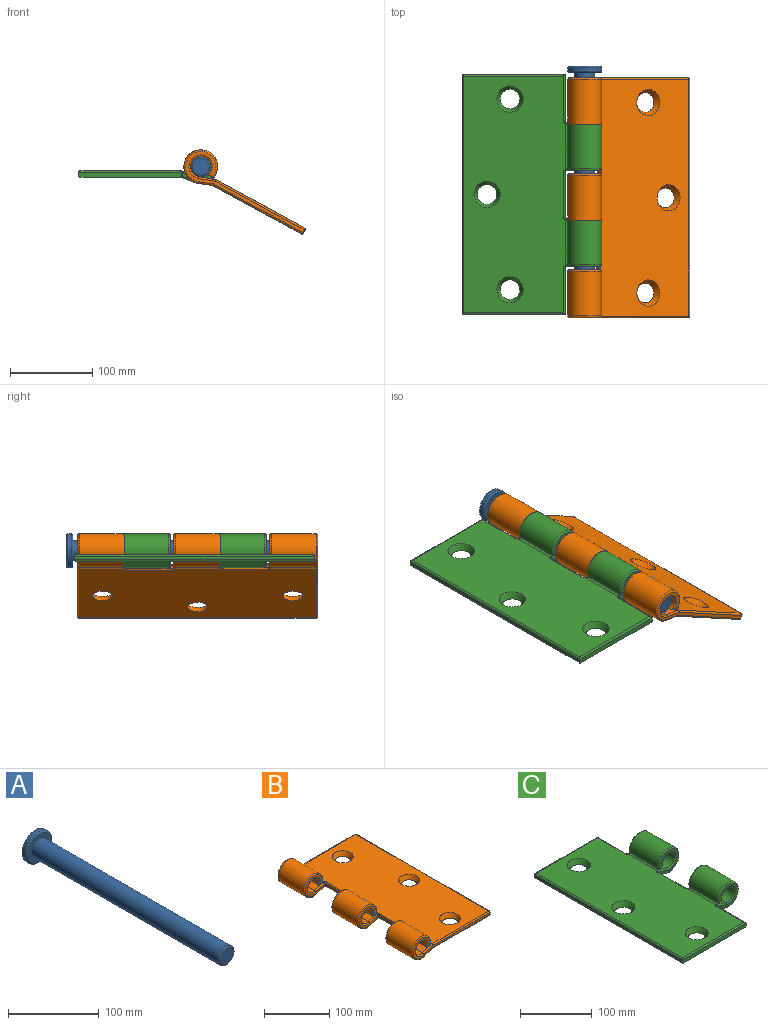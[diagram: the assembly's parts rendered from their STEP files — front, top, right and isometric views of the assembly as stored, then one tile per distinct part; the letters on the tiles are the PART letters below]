
ASSEMBLY  parts=3 mates=2
PART A: 8 faces, bbox 44.4x300x44.4 mm
  f0: cylinder r=12.25mm len=290mm, axis (0,1,0), area 22321mm2, adj f4,f7
  f1: plane 20.5x20.5mm, normal (0,-1,0), area 330.1mm2, adj f7
  f2: cylinder r=20.5mm len=41mm, axis (0,-1,0), area 515.2mm2, adj f5,f6
  f3: plane 37x37mm, normal (0,1,0), area 1075.2mm2, adj f6
  f4: plane 37x37mm, normal (0,-1,0), area 603.8mm2, adj f0,f5
  f5: torus R=18.5mm, axis (0,1,0), area 390.3mm2, adj f2,f4
  f6: torus R=18.5mm, axis (0,1,0), area 390.3mm2, adj f2,f3
  f7: torus R=10.25mm, axis (0,1,0), area 227.5mm2, adj f0,f1
PART B: 95 faces, bbox 171.6x292.4x44.8 mm
  f0: plane 55.23x16.89mm, normal (0.35,0,-0.94), area 979.8mm2, adj f2,f6,f48,f50,f67,f69
  f1: plane 57.36x19.94mm, normal (-0.32,0,0.95), area 1149.3mm2, adj f10,f13,f36,f38,f40,f57,f59
  f2: plane 288.45x123.49mm, normal (0,0,-1), area 33934.5mm2, adj f0,f3,f4,f20,f21,f22,f47,f49
  f3: plane 54.55x16.89mm, normal (0.35,0,-0.94), area 979.3mm2, adj f2,f5,f45,f47,f77
  f4: plane 55.08x16.89mm, normal (0.35,0,-0.94), area 979.7mm2, adj f2,f15,f66,f68,f87
  f5: cylinder r=20.5mm len=54.4mm, axis (0,1,0), area 5924.3mm2, adj f3,f7,f43,f75
  f6: cylinder r=20.5mm len=54.4mm, axis (0,1,0), area 5924.3mm2, adj f0,f8,f46,f65
  f7: plane 54.4x8.42mm, normal (0,0,-1), area 458.3mm2, adj f5,f9,f41,f73
  f8: plane 54.4x8.42mm, normal (0,0,-1), area 458.3mm2, adj f6,f10,f44,f63
  f9: cylinder r=12.5mm len=54.4mm, axis (0,1,0), area 3708.6mm2, adj f7,f11,f39,f74
  f10: cylinder r=12.5mm len=54.4mm, axis (0,1,0), area 3708.6mm2, adj f1,f8,f42,f61
  f11: plane 55.16x19.94mm, normal (-0.32,0,0.95), area 1146.9mm2, adj f9,f13,f33,f35,f37,f76
  f12: plane 56.6x19.94mm, normal (-0.32,0,0.95), area 1148.6mm2, adj f13,f17,f56,f58,f84
  f13: plane 288.06x123.06mm, normal (0,0,1), area 32879mm2, adj f1,f11,f12,f20,f21,f22,f33,f34
  f14: plane 288x4mm, normal (1,0,0), area 1152mm2, adj f81,f89,f90,f94
  f15: cylinder r=20.5mm len=54.4mm, axis (0,1,0), area 5924.3mm2, adj f4,f16,f64,f83
  f16: plane 54.4x8.42mm, normal (0,0,-1), area 458.3mm2, adj f15,f17,f62,f78
  f17: cylinder r=12.5mm len=54.4mm, axis (0,1,0), area 3708.6mm2, adj f12,f16,f60,f79
  f18: plane 165.48x37mm, normal (0,-1,0), area 911.5mm2, adj f78,f79,f83,f84,f87,f88,f91,f94
  f19: plane 165.48x37mm, normal (0,1,0), area 911.5mm2, adj f73,f74,f75,f76,f77,f80,f81,f82
  f20: cone r=12mm half-angle=26.6deg, axis (0,0,1), area 786.8mm2, adj f2,f13
  f21: cone r=12mm half-angle=26.6deg, axis (0,0,1), area 786.8mm2, adj f2,f13
  f22: cone r=12mm half-angle=26.6deg, axis (0,0,1), area 786.8mm2, adj f2,f13
  f23: plane 54.4x4mm, normal (-1,0,0), area 217.6mm2, adj f31,f32,f34,f51
  f24: plane 40.71x37mm, normal (0,-1,0), area 412.7mm2, adj f31,f37,f39,f41,f43,f45
  f25: plane 40.71x37mm, normal (0,1,0), area 412.7mm2, adj f32,f40,f42,f44,f46,f48
  f26: plane 54.4x4.63mm, normal (-1,0,0), area 251.8mm2, adj f29,f30,f53,f72
  f27: plane 39.56x37mm, normal (0,-1,0), area 408.4mm2, adj f29,f59,f61,f63,f65,f67
  f28: plane 39.56x37mm, normal (0,1,0), area 408.4mm2, adj f30,f58,f60,f62,f64,f66
  f29: cylinder r=2mm len=5.26mm, axis (0,0,-1), area 12.7mm2, adj f26,f27,f55,f57,f69,f71
  f30: cylinder r=2mm len=5.26mm, axis (0,0,1), area 12.7mm2, adj f26,f28,f54,f56,f68,f70
  f31: cylinder r=2mm len=4.52mm, axis (0,0,-1), area 12.4mm2, adj f23,f24,f33,f35,f47,f49
  f32: cylinder r=2mm len=4.52mm, axis (0,0,1), area 12.4mm2, adj f23,f25,f36,f38,f50,f52
  f33: torus R=4mm, axis (0,0,-1), area 9.3mm2, adj f11,f13,f31,f34,f35
  f34: cylinder r=2mm len=54.4mm, axis (0,-1,0), area 170.9mm2, adj f13,f23,f33,f36
  f35: bspline ~2.7x2.38mm, area 5.5mm2, adj f11,f31,f33,f37
  f36: torus R=4mm, axis (0,0,-1), area 9.3mm2, adj f1,f13,f32,f34,f38
  f37: cylinder r=2mm len=18.16mm, axis (0.95,0,0.32), area 58.1mm2, adj f11,f24,f35,f39
  f38: bspline ~2.7x2.38mm, area 5.5mm2, adj f1,f32,f36,f40
  f39: torus R=14.5mm, axis (0,-1,0), area 222.3mm2, adj f9,f24,f37,f41
  f40: cylinder r=2mm len=18.16mm, axis (-0.95,0,-0.32), area 58.1mm2, adj f1,f25,f38,f42
  f41: cylinder r=2mm len=8.42mm, axis (-1,0,0), area 19.6mm2, adj f7,f24,f39,f43
  f42: torus R=14.5mm, axis (0,-1,0), area 222.3mm2, adj f10,f25,f40,f44
  f43: torus R=18.5mm, axis (0,-1,0), area 327.5mm2, adj f5,f24,f41,f45
  f44: cylinder r=2mm len=8.42mm, axis (1,0,0), area 19.6mm2, adj f8,f25,f42,f46
  f45: cylinder r=2mm len=16.49mm, axis (-0.94,0,-0.35), area 52.9mm2, adj f3,f24,f43,f47
  f46: torus R=18.5mm, axis (0,-1,0), area 327.5mm2, adj f6,f25,f44,f48
  f47: bspline ~2.4x2.13mm, area 2.8mm2, adj f2,f3,f31,f45,f49
  f48: cylinder r=2mm len=16.49mm, axis (0.94,0,0.35), area 52.9mm2, adj f0,f25,f46,f50
  f49: torus R=4mm, axis (0,0,1), area 9.7mm2, adj f2,f31,f47,f51
  f50: bspline ~2.4x2.13mm, area 2.8mm2, adj f0,f2,f32,f48,f52
  f51: cylinder r=2mm len=54.4mm, axis (0,1,0), area 170.9mm2, adj f2,f23,f49,f52
  f52: torus R=4mm, axis (0,0,1), area 9.7mm2, adj f2,f32,f50,f51
  f53: cylinder r=2mm len=54.4mm, axis (0,-1,0), area 109.1mm2, adj f13,f26,f54,f55
  f54: bspline ~2.37x1.92mm, area 2.8mm2, adj f13,f30,f53,f56
  f55: bspline ~2.37x1.92mm, area 2.8mm2, adj f13,f29,f53,f57
  f56: bspline ~3.57x3.12mm, area 9.3mm2, adj f12,f30,f54,f58
  f57: bspline ~3.94x3.32mm, area 9.3mm2, adj f1,f29,f55,f59
  f58: cylinder r=2mm len=17.01mm, axis (-0.95,0,-0.32), area 54.3mm2, adj f12,f28,f56,f60
  f59: cylinder r=2mm len=17.01mm, axis (0.95,0,0.32), area 54.3mm2, adj f1,f27,f57,f61
  f60: torus R=14.5mm, axis (0,-1,0), area 222.3mm2, adj f17,f28,f58,f62
  f61: torus R=14.5mm, axis (0,-1,0), area 222.3mm2, adj f10,f27,f59,f63
  f62: cylinder r=2mm len=8.42mm, axis (1,0,0), area 19.6mm2, adj f16,f28,f60,f64
  f63: cylinder r=2mm len=8.42mm, axis (-1,0,0), area 19.6mm2, adj f8,f27,f61,f65
  f64: torus R=18.5mm, axis (0,-1,0), area 327.5mm2, adj f15,f28,f62,f66
  f65: torus R=18.5mm, axis (0,-1,0), area 327.5mm2, adj f6,f27,f63,f67
  f66: cylinder r=2mm len=15.35mm, axis (0.94,0,0.35), area 49.1mm2, adj f4,f28,f64,f68
  f67: cylinder r=2mm len=15.35mm, axis (-0.94,0,-0.35), area 49.1mm2, adj f0,f27,f65,f69
  f68: bspline ~3.61x3.08mm, area 5.9mm2, adj f4,f30,f66,f70
  f69: bspline ~3.61x3.08mm, area 5.9mm2, adj f0,f29,f67,f71
  f70: bspline ~3.87x2.48mm, area 5.3mm2, adj f2,f30,f68,f72
  f71: bspline ~3.87x2.48mm, area 5.3mm2, adj f2,f29,f69,f72
  f72: cylinder r=2mm len=54.4mm, axis (0,1,0), area 109.1mm2, adj f2,f26,f70,f71
  f73: cylinder r=2mm len=8.42mm, axis (-1,0,0), area 19.6mm2, adj f7,f19,f74,f75
  f74: torus R=14.5mm, axis (0,-1,0), area 222.3mm2, adj f9,f19,f73,f76
  f75: torus R=18.5mm, axis (0,-1,0), area 327.5mm2, adj f5,f19,f73,f77
  f76: cylinder r=2mm len=20.58mm, axis (0.95,0,0.32), area 65.7mm2, adj f11,f19,f74,f80
  f77: cylinder r=2mm len=17.91mm, axis (-0.94,0,-0.35), area 57.1mm2, adj f3,f19,f75,f82
  f78: cylinder r=2mm len=8.42mm, axis (1,0,0), area 19.6mm2, adj f16,f18,f79,f83
  f79: torus R=14.5mm, axis (0,-1,0), area 222.3mm2, adj f17,f18,f78,f84
  f80: cylinder r=2mm len=123mm, axis (1,0,0), area 385.9mm2, adj f13,f19,f76,f85
  f81: cylinder r=2mm len=4mm, axis (0,0,-1), area 12.6mm2, adj f14,f19,f85,f86
  f82: cylinder r=2mm len=123.36mm, axis (-1,0,0), area 387mm2, adj f2,f19,f77,f86
  f83: torus R=18.5mm, axis (0,-1,0), area 327.5mm2, adj f15,f18,f78,f87
  f84: cylinder r=2mm len=20.58mm, axis (-0.95,0,-0.32), area 65.7mm2, adj f12,f18,f79,f88
  f85: sphere r=2mm, area 6.3mm2, adj f80,f81,f89
  f86: sphere r=2mm, area 4mm2, adj f81,f82,f90
  f87: cylinder r=2mm len=17.91mm, axis (0.94,0,0.35), area 57.1mm2, adj f4,f18,f83,f91
  f88: cylinder r=2mm len=123mm, axis (-1,0,0), area 385.9mm2, adj f13,f18,f84,f92
  f89: cylinder r=2mm len=288mm, axis (0,1,0), area 904.8mm2, adj f13,f14,f85,f92
  f90: cylinder r=2mm len=288mm, axis (0,1,0), area 904.8mm2, adj f2,f14,f86,f93
  f91: cylinder r=2mm len=123.36mm, axis (1,0,0), area 387mm2, adj f2,f18,f87,f93
  f92: sphere r=2mm, area 6.3mm2, adj f88,f89,f94
  f93: sphere r=2mm, area 6.3mm2, adj f90,f91,f94
  f94: cylinder r=2mm len=4mm, axis (0,0,1), area 12.6mm2, adj f14,f18,f92,f93
PART C: 76 faces, bbox 171.2x292x44.4 mm
  f0: plane 54.84x16.89mm, normal (-0.35,0,-0.94), area 979.4mm2, adj f2,f12,f54,f55,f73,f75
  f1: plane 54.84x16.89mm, normal (-0.35,0,-0.94), area 979.4mm2, adj f3,f12,f31,f32,f66,f68
  f2: cylinder r=20.5mm len=54.4mm, axis (0,1,0), area 5924.3mm2, adj f0,f4,f52,f71
  f3: cylinder r=20.5mm len=54.4mm, axis (0,1,0), area 5924.3mm2, adj f1,f5,f33,f64
  f4: plane 54.4x8.42mm, normal (0,0,-1), area 458.3mm2, adj f2,f6,f50,f69
  f5: plane 54.4x8.42mm, normal (0,0,-1), area 458.3mm2, adj f3,f7,f34,f62
  f6: cylinder r=12.5mm len=54.4mm, axis (0,1,0), area 3708.6mm2, adj f4,f8,f48,f67
  f7: cylinder r=12.5mm len=54.4mm, axis (0,1,0), area 3708.6mm2, adj f5,f9,f35,f60
  f8: plane 56.23x19.94mm, normal (0.32,0,0.95), area 1148mm2, adj f6,f13,f44,f45,f46,f61,f63,f65
  f9: plane 56.23x19.94mm, normal (0.32,0,0.95), area 1148mm2, adj f7,f13,f36,f37,f38,f56,f57,f58
  f10: plane 125x6mm, normal (0,-1,0), area 748.3mm2, adj f11,f12,f19,f29,f40,f47
  f11: plane 292x4mm, normal (-1,0,0), area 1168mm2, adj f10,f14,f41,f47
  f12: plane 290x123.06mm, normal (0,0,-1), area 33962.8mm2, adj f0,f1,f10,f15,f16,f17,f29,f30
  f13: plane 288x123mm, normal (0,0,1), area 32665.2mm2, adj f8,f9,f15,f16,f17,f38,f39,f40
  f14: plane 125x4mm, normal (0,1,0), area 500mm2, adj f11,f24,f42,f49
  f15: cone r=12mm half-angle=26.6deg, axis (0,0,1), area 786.8mm2, adj f12,f13
  f16: cone r=12mm half-angle=26.6deg, axis (0,0,1), area 786.8mm2, adj f12,f13
  f17: cone r=12mm half-angle=26.6deg, axis (0,0,1), area 786.8mm2, adj f12,f13
  f18: plane 40.48x37mm, normal (0,-1,0), area 411.9mm2, adj f25,f32,f33,f34,f35,f36
  f19: plane 56.4x4mm, normal (1,0,0), area 225.6mm2, adj f10,f25,f29,f39
  f20: plane 40.48x37mm, normal (0,-1,0), area 411.9mm2, adj f26,f65,f67,f69,f71,f73
  f21: plane 40.48x37mm, normal (0,1,0), area 411.9mm2, adj f27,f58,f60,f62,f64,f66
  f22: plane 54.4x4mm, normal (1,0,0), area 217.6mm2, adj f26,f27,f59,f72
  f23: plane 40.48x37mm, normal (0,1,0), area 411.9mm2, adj f28,f46,f48,f50,f52,f54
  f24: plane 56.4x4mm, normal (1,0,0), area 225.6mm2, adj f14,f28,f43,f51
  f25: cylinder r=2mm len=4.61mm, axis (0,0,-1), area 12.3mm2, adj f18,f19,f30,f31,f37,f38
  f26: cylinder r=2mm len=4.61mm, axis (0,0,-1), area 12.3mm2, adj f20,f22,f61,f63,f74,f75
  f27: cylinder r=2mm len=4.61mm, axis (0,0,1), area 12.3mm2, adj f21,f22,f56,f57,f68,f70
  f28: cylinder r=2mm len=4.61mm, axis (0,0,1), area 12.3mm2, adj f23,f24,f44,f45,f53,f55
  f29: cylinder r=2mm len=56.4mm, axis (0,-1,0), area 177.2mm2, adj f10,f12,f19,f30
  f30: torus R=4mm, axis (0,0,1), area 9.2mm2, adj f12,f25,f29,f31
  f31: bspline ~2.48x2.34mm, area 3.4mm2, adj f1,f12,f25,f30,f32
  f32: cylinder r=2mm len=16.27mm, axis (-0.94,0,0.35), area 52.2mm2, adj f1,f18,f31,f33
  f33: torus R=18.5mm, axis (0,1,0), area 327.5mm2, adj f3,f18,f32,f34
  f34: cylinder r=2mm len=8.42mm, axis (-1,0,0), area 19.6mm2, adj f5,f18,f33,f35
  f35: torus R=14.5mm, axis (0,1,0), area 222.3mm2, adj f7,f18,f34,f36
  f36: cylinder r=2mm len=17.94mm, axis (0.95,0,-0.32), area 57.4mm2, adj f9,f18,f35,f37
  f37: bspline ~2.77x2.55mm, area 6mm2, adj f9,f25,f36,f38
  f38: torus R=4mm, axis (0,0,-1), area 8.7mm2, adj f9,f13,f25,f37,f39
  f39: cylinder r=2mm len=56.4mm, axis (0,-1,0), area 174mm2, adj f13,f19,f38,f40
  f40: cylinder r=2mm len=125mm, axis (1,0,0), area 386.4mm2, adj f10,f13,f39,f41
  f41: cylinder r=2mm len=292mm, axis (0,1,0), area 911.1mm2, adj f11,f13,f40,f42
  f42: cylinder r=2mm len=125mm, axis (-1,0,0), area 386.4mm2, adj f13,f14,f41,f43
  f43: cylinder r=2mm len=56.4mm, axis (0,1,0), area 174mm2, adj f13,f24,f42,f44
  f44: torus R=4mm, axis (0,0,-1), area 8.7mm2, adj f8,f13,f28,f43,f45
  f45: bspline ~3.65x3.14mm, area 6mm2, adj f8,f28,f44,f46
  f46: cylinder r=2mm len=17.94mm, axis (-0.95,0,0.32), area 57.4mm2, adj f8,f23,f45,f48
  f47: cylinder r=2mm len=292mm, axis (0,1,0), area 914.2mm2, adj f10,f11,f12,f49
  f48: torus R=14.5mm, axis (0,1,0), area 222.3mm2, adj f6,f23,f46,f50
  f49: cylinder r=2mm len=125mm, axis (1,0,0), area 386.4mm2, adj f12,f14,f47,f51
  f50: cylinder r=2mm len=8.42mm, axis (1,0,0), area 19.6mm2, adj f4,f23,f48,f52
  f51: cylinder r=2mm len=56.4mm, axis (0,-1,0), area 174mm2, adj f12,f24,f49,f53
  f52: torus R=18.5mm, axis (0,1,0), area 327.5mm2, adj f2,f23,f50,f54
  f53: torus R=4mm, axis (0,0,1), area 9.2mm2, adj f12,f28,f51,f55
  f54: cylinder r=2mm len=16.27mm, axis (0.94,0,-0.35), area 52.2mm2, adj f0,f23,f52,f55
  f55: bspline ~2.48x2.34mm, area 3.4mm2, adj f0,f12,f28,f53,f54
  f56: bspline ~3.65x3.14mm, area 6mm2, adj f9,f27,f57,f58
  f57: torus R=4mm, axis (0,0,-1), area 8.7mm2, adj f9,f13,f27,f56,f59
  f58: cylinder r=2mm len=17.94mm, axis (-0.95,0,0.32), area 57.4mm2, adj f9,f21,f56,f60
  f59: cylinder r=2mm len=54.4mm, axis (0,-1,0), area 170.9mm2, adj f13,f22,f57,f61
  f60: torus R=14.5mm, axis (0,1,0), area 222.3mm2, adj f7,f21,f58,f62
  f61: torus R=4mm, axis (0,0,-1), area 8.7mm2, adj f8,f13,f26,f59,f63
  f62: cylinder r=2mm len=8.42mm, axis (1,0,0), area 19.6mm2, adj f5,f21,f60,f64
  f63: bspline ~3.65x3.14mm, area 6mm2, adj f8,f26,f61,f65
  f64: torus R=18.5mm, axis (0,1,0), area 327.5mm2, adj f3,f21,f62,f66
  f65: cylinder r=2mm len=17.94mm, axis (0.95,0,-0.32), area 57.4mm2, adj f8,f20,f63,f67
  f66: cylinder r=2mm len=16.27mm, axis (0.94,0,-0.35), area 52.2mm2, adj f1,f21,f64,f68
  f67: torus R=14.5mm, axis (0,1,0), area 222.3mm2, adj f6,f20,f65,f69
  f68: bspline ~2.48x2.34mm, area 3.4mm2, adj f1,f12,f27,f66,f70
  f69: cylinder r=2mm len=8.42mm, axis (-1,0,0), area 19.6mm2, adj f4,f20,f67,f71
  f70: torus R=4mm, axis (0,0,1), area 9.2mm2, adj f12,f27,f68,f72
  f71: torus R=18.5mm, axis (0,1,0), area 327.5mm2, adj f2,f20,f69,f73
  f72: cylinder r=2mm len=54.4mm, axis (0,-1,0), area 170.9mm2, adj f12,f22,f70,f74
  f73: cylinder r=2mm len=16.27mm, axis (-0.94,0,0.35), area 52.2mm2, adj f0,f20,f71,f75
  f74: torus R=4mm, axis (0,0,1), area 9.2mm2, adj f12,f26,f72,f75
  f75: bspline ~2.48x2.34mm, area 3.4mm2, adj f0,f12,f26,f73,f74
PLACE A rot(axis=(0,1,0),28.6deg) t=(-184.96,-163.51,-75.82)mm
PLACE B rot(axis=(0,1,0),28.6deg) t=(-184.96,-169.51,-75.82)mm
PLACE C t=(-184.59,-165.51,-88.41)mm fixed
MATE revolute B.f42 <-> C.f2  axis (0,-1,0) through (-160.6,-342.71,-83.41)mm
MATE slider A.f0 <-> B.f5  axis (0,-1,0) through (-160.6,-455.51,-83.41)mm
